# Revit family: ВКМц_Eng
name_source: partatom
category: Mechanical Equipment
units: mm (PartAtom-declared; Revit-internal decimal feet)

## family parameters
Always vertical = Yes
Classification = None
Cut with Voids When Loaded = No
Part Type = Normal
Room Calculation Point = No
Round Connector Dimension = Use Diameter
Shared = No
Work Plane-Based = No

## types (13) — shared parameters
00_20_Manufacturer = Vents
00_20_Name = Inline centrifugal fan
Casing Material = Steel, galvanized
Frequency = 50 Hz
Load Classification = HVAC
Maintenance zone material = <By Category>
Manufacturer = Vents
Number of Fase = 1
Pressure_Static_Air = 0.0 Pa
URL = https://ventilation-system.com
Voltage = 230 V
zero-valued in all types: Default Elevation

## per-type parameters (varying)
- VKMz 100 Q: Amperage=0 A; Apparent Load=44 VA; B=253 mm; B1=293 mm; B2=213 mm; D1=237 mm; D2=212 mm; Diameter=100 mm  [stored 0.328084 ft]; Dy=100 mm  [stored 0.328084 ft]; H1=169 mm; Height=287 mm; L=202 mm; L1=23 mm  [stored 0.0754593 ft]; L2=22 mm  [stored 0.0721785 ft]; L3=30 mm  [stored 0.0984252 ft]; L4=62 mm  [stored 0.203412 ft]; L5=41 mm; L6=87 mm  [stored 0.285433 ft]; L7=40 mm  [stored 0.131234 ft]; L8=92 mm  [stored 0.301837 ft]; Length=202 mm; Power=42 W; R1=119 mm; R2=124 mm  [stored 0.406824 ft]; Ry=50 mm  [stored 0.164042 ft]; Sound pressure level at 3 m distance=35 dBA; Temperature of moving air=-25...+55°C; Weight=2.50 kg; Width=293 mm
- VKMz 315: Amperage=1 A; Apparent Load=186 VA; B=410 mm; B1=450 mm; B2=370 mm; D1=402 mm; D2=377 mm; Diameter=315 mm; Dy=315 mm; H1=251 mm; Height=452 mm; L=308 mm; L1=33 mm  [stored 0.108268 ft]; L2=55 mm  [stored 0.180446 ft]; L3=40 mm  [stored 0.131234 ft]; L4=95 mm  [stored 0.31168 ft]; L5=74 mm; L6=120 mm  [stored 0.393701 ft]; L7=50 mm  [stored 0.164042 ft]; L8=125 mm; Length=308 mm; Power=185 W; R1=201 mm; R2=206 mm; Ry=158 mm; Sound pressure level at 3 m distance=53 dBA; Temperature of moving air=-25...+45°C; Weight=6.50 kg; Width=450 mm
- VKMz 100: Amperage=0 A; Apparent Load=64 VA; B=253 mm; B1=293 mm; B2=213 mm; D1=237 mm; D2=212 mm; Diameter=100 mm  [stored 0.328084 ft]; Dy=100 mm  [stored 0.328084 ft]; H1=169 mm; Height=287 mm; L=202 mm; L1=23 mm  [stored 0.0754593 ft]; L2=22 mm  [stored 0.0721785 ft]; L3=30 mm  [stored 0.0984252 ft]; L4=62 mm  [stored 0.203412 ft]; L5=41 mm; L6=87 mm  [stored 0.285433 ft]; L7=40 mm  [stored 0.131234 ft]; L8=92 mm  [stored 0.301837 ft]; Length=202 mm; Power=62 W; R1=119 mm; R2=124 mm  [stored 0.406824 ft]; Ry=50 mm  [stored 0.164042 ft]; Sound pressure level at 3 m distance=46 dBA; Temperature of moving air=-25...+55°C; Weight=2.80 kg; Width=293 mm
- VKMz 125 Q: Amperage=0 A; Apparent Load=85 VA; B=253 mm; B1=293 mm; B2=213 mm; D1=237 mm; D2=212 mm; Diameter=125 mm; Dy=125 mm; H1=169 mm; Height=287 mm; L=202 mm; L1=23 mm  [stored 0.0754593 ft]; L2=22 mm  [stored 0.0721785 ft]; L3=30 mm  [stored 0.0984252 ft]; L4=62 mm  [stored 0.203412 ft]; L5=41 mm; L6=87 mm  [stored 0.285433 ft]; L7=40 mm  [stored 0.131234 ft]; L8=92 mm  [stored 0.301837 ft]; Length=202 mm; Power=60 W; R1=119 mm; R2=124 mm  [stored 0.406824 ft]; Ry=63 mm; Sound pressure level at 3 m distance=35 dBA; Temperature of moving air=-25...+55°C; Weight=2.70 kg; Width=293 mm
- VKMz 125: Amperage=0 A; Apparent Load=78 VA; B=253 mm; B1=293 mm; B2=213 mm; D1=237 mm; D2=212 mm; Diameter=125 mm; Dy=125 mm; H1=169 mm; Height=287 mm; L=202 mm; L1=23 mm  [stored 0.0754593 ft]; L2=22 mm  [stored 0.0721785 ft]; L3=30 mm  [stored 0.0984252 ft]; L4=62 mm  [stored 0.203412 ft]; L5=41 mm; L6=87 mm  [stored 0.285433 ft]; L7=40 mm  [stored 0.131234 ft]; L8=92 mm  [stored 0.301837 ft]; Length=202 mm; Power=78 W; R1=119 mm; R2=124 mm  [stored 0.406824 ft]; Ry=63 mm; Sound pressure level at 3 m distance=46 dBA; Temperature of moving air=-25...+55°C; Weight=2.90 kg; Width=293 mm
- VKMz 150: Amperage=0 A; Apparent Load=67 VA; B=290 mm; B1=330 mm; B2=250 mm; D1=274 mm; D2=249 mm; Diameter=150 mm; Dy=150 mm; H1=187 mm; Height=324 mm; L=170 mm; L1=20 mm  [stored 0.0656168 ft]; L2=20 mm  [stored 0.0656168 ft]; L3=30 mm  [stored 0.0984252 ft]; L4=52 mm; L5=31 mm; L6=77 mm  [stored 0.252625 ft]; L7=40 mm  [stored 0.131234 ft]; L8=82 mm  [stored 0.269029 ft]; Length=170 mm; Power=64 W; R1=137 mm; R2=142 mm; Ry=75 mm; Sound pressure level at 3 m distance=44 dBA; Temperature of moving air=-25...+50°C; Weight=3.20 kg; Width=330 mm
- VKMSz 150: Amperage=1 A; Apparent Load=129 VA; B=355 mm; B1=395 mm; B2=315 mm; D1=345 mm; D2=320 mm; Diameter=150 mm; Dy=150 mm; H1=223 mm; Height=395 mm; L=230 mm; L1=20 mm  [stored 0.0656168 ft]; L2=20 mm  [stored 0.0656168 ft]; L3=40 mm  [stored 0.131234 ft]; L4=82 mm  [stored 0.269029 ft]; L5=61 mm; L6=107 mm  [stored 0.35105 ft]; L7=50 mm  [stored 0.164042 ft]; L8=112 mm  [stored 0.367454 ft]; Length=230 mm; Power=127 W; R1=173 mm; R2=178 mm; Ry=75 mm; Sound pressure level at 3 m distance=48 dBA; Temperature of moving air=-25...+60°C; Weight=4.80 kg; Width=395 mm
- VKMz 160: Amperage=0 A; Apparent Load=78 VA; B=294 mm; B1=334 mm; B2=254 mm; D1=278 mm; D2=253 mm; Diameter=160 mm; Dy=160 mm; H1=189 mm; Height=328 mm; L=200 mm; L1=25 mm  [stored 0.082021 ft]; L2=23 mm  [stored 0.0754593 ft]; L3=30 mm  [stored 0.0984252 ft]; L4=57 mm  [stored 0.187008 ft]; L5=36 mm; L6=82 mm  [stored 0.269029 ft]; L7=40 mm  [stored 0.131234 ft]; L8=87 mm  [stored 0.285433 ft]; Length=200 mm; Power=78 W; R1=139 mm; R2=144 mm; Ry=80 mm  [stored 0.262467 ft]; Sound pressure level at 3 m distance=46 dBA; Temperature of moving air=-25...+55°C; Weight=3.20 kg; Width=334 mm
- VKMz 200 Q: Amperage=1 A; Apparent Load=140 VA; B=340 mm; B1=380 mm; B2=300 mm; D1=332 mm; D2=307 mm; Diameter=200 mm; Dy=200 mm; H1=216 mm; Height=382 mm; L=245 mm; L1=25 mm  [stored 0.082021 ft]; L2=29 mm  [stored 0.0951444 ft]; L3=40 mm  [stored 0.131234 ft]; L4=80 mm  [stored 0.262467 ft]; L5=58 mm  [stored 0.190289 ft]; L6=105 mm; L7=50 mm  [stored 0.164042 ft]; L8=110 mm  [stored 0.360892 ft]; Length=245 mm; Power=139 W; R1=166 mm; R2=171 mm; Ry=100 mm  [stored 0.328084 ft]; Sound pressure level at 3 m distance=48 dBA; Temperature of moving air=-25...+50°C; Weight=5.20 kg; Width=380 mm
- VKMz 250 Q: Amperage=1 A; Apparent Load=136 VA; B=340 mm; B1=380 mm; B2=300 mm; D1=332 mm; D2=307 mm; Diameter=250 mm; Dy=250 mm; H1=216 mm; Height=382 mm; L=213 mm; L1=25 mm  [stored 0.082021 ft]; L2=29 mm  [stored 0.0951444 ft]; L3=40 mm  [stored 0.131234 ft]; L4=64 mm  [stored 0.209974 ft]; L5=42 mm  [stored 0.137795 ft]; L6=89 mm; L7=50 mm  [stored 0.164042 ft]; L8=94 mm; Length=213 mm; Power=134 W; R1=166 mm; R2=171 mm; Ry=125 mm; Sound pressure level at 3 m distance=51 dBA; Temperature of moving air=-25...+50°C; Weight=5.10 kg; Width=380 mm
- VKMz 250: Amperage=1 A; Apparent Load=159 VA; B=340 mm; B1=380 mm; B2=300 mm; D1=332 mm; D2=307 mm; Diameter=250 mm; Dy=250 mm; H1=216 mm; Height=382 mm; L=213 mm; L1=25 mm  [stored 0.082021 ft]; L2=29 mm  [stored 0.0951444 ft]; L3=40 mm  [stored 0.131234 ft]; L4=64 mm  [stored 0.209974 ft]; L5=42 mm  [stored 0.137795 ft]; L6=89 mm; L7=50 mm  [stored 0.164042 ft]; L8=94 mm; Length=213 mm; Power=157 W; R1=166 mm; R2=171 mm; Ry=125 mm; Sound pressure level at 3 m distance=50 dBA; Temperature of moving air=-25...+50°C; Weight=5.10 kg; Width=380 mm
- VKMz 315 Q: Amperage=1 A; Apparent Load=152 VA; B=410 mm; B1=450 mm; B2=370 mm; D1=402 mm; D2=377 mm; Diameter=315 mm; Dy=315 mm; H1=251 mm; Height=452 mm; L=308 mm; L1=33 mm  [stored 0.108268 ft]; L2=55 mm  [stored 0.180446 ft]; L3=40 mm  [stored 0.131234 ft]; L4=95 mm  [stored 0.31168 ft]; L5=74 mm; L6=120 mm  [stored 0.393701 ft]; L7=50 mm  [stored 0.164042 ft]; L8=125 mm; Length=308 mm; Power=151 W; R1=201 mm; R2=206 mm; Ry=158 mm; Sound pressure level at 3 m distance=52 dBA; Temperature of moving air=-25...+50°C; Weight=6.50 kg; Width=450 mm
- VKMz 200: Amperage=1 A; Apparent Load=159 VA; B=340 mm; B1=380 mm; B2=300 mm; D1=332 mm; D2=307 mm; Diameter=200 mm; Dy=200 mm; H1=216 mm; Height=382 mm; L=245 mm; L1=25 mm  [stored 0.082021 ft]; L2=29 mm  [stored 0.0951444 ft]; L3=40 mm  [stored 0.131234 ft]; L4=80 mm  [stored 0.262467 ft]; L5=58 mm  [stored 0.190289 ft]; L6=105 mm; L7=50 mm  [stored 0.164042 ft]; L8=110 mm  [stored 0.360892 ft]; Length=245 mm; Power=157 W; R1=166 mm; R2=171 mm; Ry=100 mm  [stored 0.328084 ft]; Sound pressure level at 3 m distance=50 dBA; Temperature of moving air=-25...+50°C; Weight=5.20 kg; Width=380 mm

note: column(s) folded — value = type name in every type: 00_20_Type

note: [stored X ft] marks values corroborated as IEEE doubles in the binary element streams (Revit-internal decimal feet)
